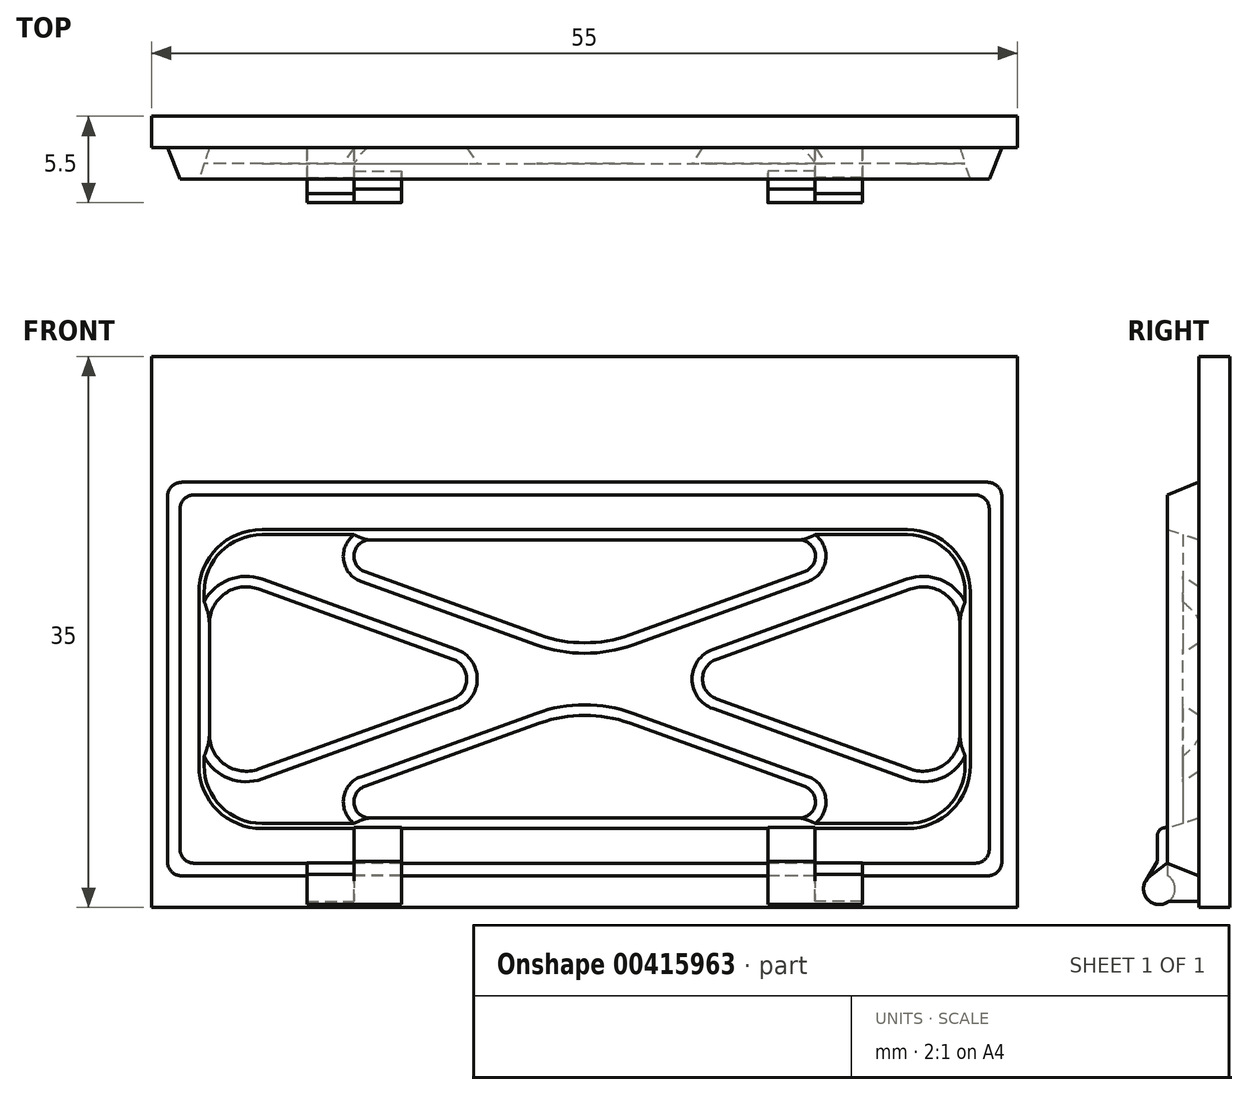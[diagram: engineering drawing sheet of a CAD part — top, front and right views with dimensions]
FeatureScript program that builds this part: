
annotation { "Feature Type Name" : "Feature", "Feature Type Description" : "" }
export const myFeature = defineFeature(function(context is Context, id is Id, definition is map)
    precondition{}
    {
        {
            var Q0;
            Q0=qCreatedBy(makeId("Front.planeOp"),FACE);
            var sketch = newSketch(context, id + "F0", { "sketchPlane" : qUnion([Q0])});
            skLineSegment(sketch, "E0.bottom", {"start": v(-23.45, 22) * mm, "end": v(31.55, 22) * mm});
            skLineSegment(sketch, "E0.top", {"start": v(-23.45, -13) * mm, "end": v(31.55, -13) * mm});
            skLineSegment(sketch, "E0.left", {"start": v(-23.45, 22) * mm, "end": v(-23.45, -13) * mm});
            skLineSegment(sketch, "E0.right", {"start": v(31.55, 22) * mm, "end": v(31.55, -13) * mm});
            skSolve(sketch);
        }
        {
            var Q0;
            Q0=makeQuery(id+"F0.imprint","IMPRINT",FACE,{"disambiguationData":[TD([[makeQuery(id+"F0.imprint","IMPRINT",EDGE,{"derivedFrom":sQuery(id+"F0.wireOp",EDGE,"E0.bottom")}),-1.0]])]});
            extrude(context, id + "F1", {"entities" : qUnion([Q0]), "depth" : 2 * mm, "offsetDistance" : 25 * mm});
        }
        {
            var Q0;
            Q0=makeQuery(id+"F1.opExtrude","CAP_FACE",FACE,{"disambiguationData":[OSD([sQuery(id+"F0.wireOp",EDGE,"E0.bottom"),sQuery(id+"F0.wireOp",EDGE,"E0.top"),sQuery(id+"F0.wireOp",EDGE,"E0.left"),sQuery(id+"F0.wireOp",EDGE,"E0.right")])],"isStart":false});
            var sketch = newSketch(context, id + "F2", { "sketchPlane" : qUnion([Q0])});
            skLineSegment(sketch, "E1", {"start": v(30.55, -11) * mm, "end": v(30.55, 14) * mm});
            skLineSegment(sketch, "E2", {"start": v(-22.45, -11) * mm, "end": v(-22.45, 14) * mm});
            skLineSegment(sketch, "E3", {"start": v(-22.45, 14) * mm, "end": v(30.55, 14) * mm});
            skLineSegment(sketch, "E4", {"start": v(30.55, -11) * mm, "end": v(-22.45, -11) * mm});
            skLineSegment(sketch, "E5.0", {"start": v(-19.45, 10) * mm, "end": v(27.55, 10) * mm});
            skLineSegment(sketch, "E6.0", {"start": v(-19.45, -7) * mm, "end": v(27.55, -7) * mm});
            skLineSegment(sketch, "E7.0", {"start": v(-19.45, 10) * mm, "end": v(-19.45, -7) * mm});
            skLineSegment(sketch, "E8.0", {"start": v(27.55, -7) * mm, "end": v(27.55, 10) * mm});
            skSolve(sketch);
        }
        {
            var Q0;
            Q0=makeQuery(id+"F2.imprint","IMPRINT",FACE,{"disambiguationData":[TD([[makeQuery(id+"F2.imprint","IMPRINT",EDGE,{"derivedFrom":sQuery(id+"F2.wireOp",EDGE,"E1")}),1.0]])]});
            extrude(context, id + "F3", {"entities" : qUnion([Q0]), "operationType" : NewBodyOperationType.ADD, "depth" : 2 * mm, "offsetDistance" : 25 * mm});
        }
        {
            var Q0;
            Q0=makeQuery(id+"F3.boolean.opBoolean","SPLIT",FACE,{"disambiguationData":[TD([makeQuery(id+"F3.opExtrude","SWEPT_FACE",FACE,{"disambiguationData":[OSD([sQuery(id+"F2.wireOp",EDGE,"E5.0")])]})])],"derivedFrom":makeQuery(id+"F1.opExtrude","CAP_FACE",FACE,{"disambiguationData":[OSD([sQuery(id+"F0.wireOp",EDGE,"E0.bottom"),sQuery(id+"F0.wireOp",EDGE,"E0.top"),sQuery(id+"F0.wireOp",EDGE,"E0.left"),sQuery(id+"F0.wireOp",EDGE,"E0.right")])],"isStart":false})});
            var sketch = newSketch(context, id + "F4", { "sketchPlane" : qUnion([Q0])});
            skLineSegment(sketch, "E9.bottom", {"start": v(-19.45, 10) * mm, "end": v(27.55, 10) * mm});
            skLineSegment(sketch, "E9.top", {"start": v(-19.45, -7) * mm, "end": v(27.55, -7) * mm});
            skLineSegment(sketch, "E9.left", {"start": v(-19.45, 10) * mm, "end": v(-19.45, -7) * mm});
            skLineSegment(sketch, "E9.right", {"start": v(27.55, 10) * mm, "end": v(27.55, -7) * mm});
            skLineSegment(sketch, "E10", {"start": v(-19.45, 10) * mm, "end": v(27.55, -7) * mm});
            skLineSegment(sketch, "E11", {"start": v(27.55, 10) * mm, "end": v(-19.45, -7) * mm});
            skLineSegment(sketch, "E12.0", {"start": v(-19.45, 7.87) * mm, "end": v(21.67, -7) * mm});
            skLineSegment(sketch, "E13.0", {"start": v(-13.57, 10) * mm, "end": v(27.55, -4.87) * mm});
            skLineSegment(sketch, "E14.0", {"start": v(21.67, 10) * mm, "end": v(-19.45, -4.87) * mm});
            skLineSegment(sketch, "E15.0", {"start": v(27.55, 7.87) * mm, "end": v(-13.57, -7) * mm});
            skLineSegment(sketch, "E16.0", {"start": v(-20.45, 11) * mm, "end": v(28.55, 11) * mm});
            skLineSegment(sketch, "E16.1", {"start": v(-20.45, 11) * mm, "end": v(-20.45, -8) * mm});
            skLineSegment(sketch, "E16.2", {"start": v(-20.45, -8) * mm, "end": v(28.55, -8) * mm});
            skLineSegment(sketch, "E16.3", {"start": v(28.55, 11) * mm, "end": v(28.55, -8) * mm});
            skSolve(sketch);
        }
        {
            var Q0;
            {var subQ1=sQuery(id+"F4.wireOp",EDGE,"E9.left");var subQ3=sQuery(id+"F4.wireOp",EDGE,"E12.0");var subQ4=makeQuery(id+"F4.imprint","INTERSECT",VERTEX,{"derivedFrom":[subQ1,subQ3]});Q0=makeQuery(id+"F4.imprint","IMPRINT",FACE,{"disambiguationData":[TD([[makeQuery(id+"F4.imprint","IMPRINT",EDGE,{"disambiguationData":[TD([[subQ4,-1.0]])],"derivedFrom":subQ3}),1.0]])]});}
            var Q1;
            {var subQ1=sQuery(id+"F4.wireOp",EDGE,"E9.bottom");var subQ3=sQuery(id+"F4.wireOp",EDGE,"E13.0");var subQ4=makeQuery(id+"F4.imprint","INTERSECT",VERTEX,{"derivedFrom":[subQ1,subQ3]});Q1=makeQuery(id+"F4.imprint","IMPRINT",FACE,{"disambiguationData":[TD([[makeQuery(id+"F4.imprint","IMPRINT",EDGE,{"disambiguationData":[TD([[subQ4,-1.0]])],"derivedFrom":subQ3}),-1.0]])]});}
            var Q2;
            {var subQ0=sQuery(id+"F4.wireOp",EDGE,"E14.0");var subQ1=sQuery(id+"F4.wireOp",EDGE,"E10");var subQ2=makeQuery(id+"F4.imprint","INTERSECT",VERTEX,{"derivedFrom":[subQ1,subQ0]});Q2=makeQuery(id+"F4.imprint","IMPRINT",FACE,{"disambiguationData":[TD([[makeQuery(id+"F4.imprint","IMPRINT",EDGE,{"disambiguationData":[TD([[subQ2,-1.0]])],"derivedFrom":subQ1}),1.0]])]});}
            var Q3;
            {var subQ0=sQuery(id+"F4.wireOp",EDGE,"E11");var subQ1=sQuery(id+"F4.wireOp",EDGE,"E10");var subQ2=makeQuery(id+"F4.imprint","INTERSECT",VERTEX,{"derivedFrom":[subQ1,subQ0]});Q3=makeQuery(id+"F4.imprint","IMPRINT",FACE,{"disambiguationData":[TD([[makeQuery(id+"F4.imprint","IMPRINT",EDGE,{"disambiguationData":[TD([[subQ2,-1.0]])],"derivedFrom":subQ1}),-1.0]])]});}
            var Q4;
            {var subQ0=sQuery(id+"F4.wireOp",EDGE,"E11");var subQ1=sQuery(id+"F4.wireOp",EDGE,"E10");var subQ2=makeQuery(id+"F4.imprint","INTERSECT",VERTEX,{"derivedFrom":[subQ1,subQ0]});Q4=makeQuery(id+"F4.imprint","IMPRINT",FACE,{"disambiguationData":[TD([[makeQuery(id+"F4.imprint","IMPRINT",EDGE,{"disambiguationData":[TD([[subQ2,-1.0]])],"derivedFrom":subQ1}),1.0]])]});}
            var Q5;
            {var subQ0=sQuery(id+"F4.wireOp",EDGE,"E14.0");var subQ1=sQuery(id+"F4.wireOp",EDGE,"E10");var subQ2=makeQuery(id+"F4.imprint","INTERSECT",VERTEX,{"derivedFrom":[subQ1,subQ0]});Q5=makeQuery(id+"F4.imprint","IMPRINT",FACE,{"disambiguationData":[TD([[makeQuery(id+"F4.imprint","IMPRINT",EDGE,{"disambiguationData":[TD([[subQ2,-1.0]])],"derivedFrom":subQ1}),-1.0]])]});}
            var Q6;
            {var subQ0=sQuery(id+"F4.wireOp",EDGE,"E11");var subQ5=sQuery(id+"F4.wireOp",EDGE,"E12.0");var subQ6=makeQuery(id+"F4.imprint","INTERSECT",VERTEX,{"derivedFrom":[subQ0,subQ5]});Q6=makeQuery(id+"F4.imprint","IMPRINT",FACE,{"disambiguationData":[TD([[makeQuery(id+"F4.imprint","IMPRINT",EDGE,{"disambiguationData":[TD([[subQ6,-1.0]])],"derivedFrom":subQ5}),-1.0]])]});}
            var Q7;
            {var subQ0=sQuery(id+"F4.wireOp",EDGE,"E11");var subQ5=sQuery(id+"F4.wireOp",EDGE,"E13.0");var subQ6=makeQuery(id+"F4.imprint","INTERSECT",VERTEX,{"derivedFrom":[subQ0,subQ5]});Q7=makeQuery(id+"F4.imprint","IMPRINT",FACE,{"disambiguationData":[TD([[makeQuery(id+"F4.imprint","IMPRINT",EDGE,{"disambiguationData":[TD([[subQ6,1.0]])],"derivedFrom":subQ5}),1.0]])]});}
            var Q8;
            {var subQ0=sQuery(id+"F4.wireOp",EDGE,"E11");var subQ5=sQuery(id+"F4.wireOp",EDGE,"E13.0");var subQ6=makeQuery(id+"F4.imprint","INTERSECT",VERTEX,{"derivedFrom":[subQ0,subQ5]});Q8=makeQuery(id+"F4.imprint","IMPRINT",FACE,{"disambiguationData":[TD([[makeQuery(id+"F4.imprint","IMPRINT",EDGE,{"disambiguationData":[TD([[subQ6,-1.0]])],"derivedFrom":subQ5}),1.0]])]});}
            var Q9;
            {var subQ1=sQuery(id+"F4.wireOp",EDGE,"E9.right");var subQ3=sQuery(id+"F4.wireOp",EDGE,"E13.0");var subQ4=makeQuery(id+"F4.imprint","INTERSECT",VERTEX,{"derivedFrom":[subQ1,subQ3]});Q9=makeQuery(id+"F4.imprint","IMPRINT",FACE,{"disambiguationData":[TD([[makeQuery(id+"F4.imprint","IMPRINT",EDGE,{"disambiguationData":[TD([[subQ4,1.0]])],"derivedFrom":subQ3}),-1.0]])]});}
            var Q10;
            {var subQ1=sQuery(id+"F4.wireOp",EDGE,"E9.top");var subQ3=sQuery(id+"F4.wireOp",EDGE,"E12.0");var subQ4=makeQuery(id+"F4.imprint","INTERSECT",VERTEX,{"derivedFrom":[subQ1,subQ3]});Q10=makeQuery(id+"F4.imprint","IMPRINT",FACE,{"disambiguationData":[TD([[makeQuery(id+"F4.imprint","IMPRINT",EDGE,{"disambiguationData":[TD([[subQ4,1.0]])],"derivedFrom":subQ3}),1.0]])]});}
            var Q11;
            {var subQ0=sQuery(id+"F4.wireOp",EDGE,"E11");var subQ5=sQuery(id+"F4.wireOp",EDGE,"E12.0");var subQ6=makeQuery(id+"F4.imprint","INTERSECT",VERTEX,{"derivedFrom":[subQ0,subQ5]});Q11=makeQuery(id+"F4.imprint","IMPRINT",FACE,{"disambiguationData":[TD([[makeQuery(id+"F4.imprint","IMPRINT",EDGE,{"disambiguationData":[TD([[subQ6,1.0]])],"derivedFrom":subQ5}),-1.0]])]});}
            var Q12;
            Q12=makeQuery(id+"F4.imprint","IMPRINT",FACE,{"disambiguationData":[TD([[makeQuery(id+"F4.imprint","IMPRINT",EDGE,{"derivedFrom":sQuery(id+"F4.wireOp",EDGE,"E16.0")}),-1.0]])]});
            extrude(context, id + "F5", {"entities" : qUnion([Q0, Q1, Q2, Q3, Q4, Q5, Q6, Q7, Q8, Q9, Q10, Q11, Q12]), "depth" : 1 * mm, "offsetDistance" : 25 * mm});
        }
        {
            var Q0;
            Q0=makeQuery(id+"F5.opExtrude","SWEPT_EDGE",EDGE,{"disambiguationData":[OSD([sQuery(id+"F4.wireOp",EDGE,"E9.left"),sQuery(id+"F4.wireOp",EDGE,"E12.0")])]});
            var Q1;
            Q1=makeQuery(id+"F5.opExtrude","SWEPT_EDGE",EDGE,{"disambiguationData":[OSD([sQuery(id+"F4.wireOp",EDGE,"E9.left"),sQuery(id+"F4.wireOp",EDGE,"E14.0")])]});
            var Q2;
            Q2=makeQuery(id+"F5.opExtrude","SWEPT_EDGE",EDGE,{"disambiguationData":[OSD([sQuery(id+"F4.wireOp",EDGE,"E9.right"),sQuery(id+"F4.wireOp",EDGE,"E13.0")])]});
            var Q3;
            Q3=makeQuery(id+"F5.opExtrude","SWEPT_EDGE",EDGE,{"disambiguationData":[OSD([sQuery(id+"F4.wireOp",EDGE,"E9.right"),sQuery(id+"F4.wireOp",EDGE,"E15.0")])]});
            fillet(context, id + "F6", {"entities" : qUnion([Q0, Q1, Q2, Q3]), "radius" : 2 * mm, "tangentPropagation" : true, "allowEdgeOverflow" : false});
        }
        {
            var Q0;
            Q0=makeQuery(id+"F5.opExtrude","SWEPT_EDGE",EDGE,{"disambiguationData":[OSD([sQuery(id+"F4.wireOp",EDGE,"E9.bottom"),sQuery(id+"F4.wireOp",EDGE,"E13.0")])]});
            var Q1;
            Q1=makeQuery(id+"F5.opExtrude","SWEPT_EDGE",EDGE,{"disambiguationData":[OSD([sQuery(id+"F4.wireOp",EDGE,"E9.top"),sQuery(id+"F4.wireOp",EDGE,"E15.0")])]});
            var Q2;
            Q2=makeQuery(id+"F5.opExtrude","SWEPT_EDGE",EDGE,{"disambiguationData":[OSD([sQuery(id+"F4.wireOp",EDGE,"E9.top"),sQuery(id+"F4.wireOp",EDGE,"E12.0")])]});
            var Q3;
            Q3=makeQuery(id+"F5.opExtrude","SWEPT_EDGE",EDGE,{"disambiguationData":[OSD([sQuery(id+"F4.wireOp",EDGE,"E9.bottom"),sQuery(id+"F4.wireOp",EDGE,"E14.0")])]});
            fillet(context, id + "F7", {"entities" : qUnion([Q0, Q1, Q2, Q3]), "radius" : 0.7 * mm, "tangentPropagation" : true, "allowEdgeOverflow" : false});
        }
        {
            var Q0;
            Q0=makeQuery(id+"F5.opExtrude","SWEPT_EDGE",EDGE,{"disambiguationData":[OSD([sQuery(id+"F4.wireOp",EDGE,"E13.0"),sQuery(id+"F4.wireOp",EDGE,"E14.0")])]});
            var Q1;
            Q1=makeQuery(id+"F5.opExtrude","SWEPT_EDGE",EDGE,{"disambiguationData":[OSD([sQuery(id+"F4.wireOp",EDGE,"E12.0"),sQuery(id+"F4.wireOp",EDGE,"E15.0")])]});
            fillet(context, id + "F8", {"entities" : qUnion([Q0, Q1]), "radius" : 8 * mm, "tangentPropagation" : true, "allowEdgeOverflow" : false});
        }
        {
            var Q0;
            Q0=makeQuery(id+"F5.opExtrude","SWEPT_EDGE",EDGE,{"disambiguationData":[OSD([sQuery(id+"F4.wireOp",EDGE,"E12.0"),sQuery(id+"F4.wireOp",EDGE,"E14.0")])]});
            var Q1;
            Q1=makeQuery(id+"F5.opExtrude","SWEPT_EDGE",EDGE,{"disambiguationData":[OSD([sQuery(id+"F4.wireOp",EDGE,"E13.0"),sQuery(id+"F4.wireOp",EDGE,"E15.0")])]});
            fillet(context, id + "F9", {"entities" : qUnion([Q0, Q1]), "radius" : 1 * mm, "tangentPropagation" : true, "allowEdgeOverflow" : false});
        }
        {
            var Q0;
            {var subQ0=sQuery(id+"F4.wireOp",EDGE,"E13.0");Q0=makeQuery(id+"F5.opExtrude","CAP_EDGE",EDGE,{"disambiguationData":[OSD([subQ0]),TDD([makeQuery(id+"F4.imprint","IMPRINT",EDGE,{"disambiguationData":[TD([[makeQuery(id+"F4.imprint","INTERSECT",VERTEX,{"derivedFrom":[sQuery(id+"F4.wireOp",EDGE,"E9.bottom"),subQ0]}),-1.0]])],"derivedFrom":subQ0})])],"isStart":false});}
            var Q1;
            {var subQ0=sQuery(id+"F4.wireOp",EDGE,"E12.0");Q1=makeQuery(id+"F5.opExtrude","CAP_EDGE",EDGE,{"disambiguationData":[OSD([subQ0]),TDD([makeQuery(id+"F4.imprint","IMPRINT",EDGE,{"disambiguationData":[TD([[makeQuery(id+"F4.imprint","INTERSECT",VERTEX,{"derivedFrom":[sQuery(id+"F4.wireOp",EDGE,"E9.left"),subQ0]}),-1.0]])],"derivedFrom":subQ0})])],"isStart":false});}
            var Q2;
            {var subQ0=sQuery(id+"F4.wireOp",EDGE,"E15.0");Q2=makeQuery(id+"F5.opExtrude","CAP_EDGE",EDGE,{"disambiguationData":[OSD([subQ0]),TDD([makeQuery(id+"F4.imprint","IMPRINT",EDGE,{"disambiguationData":[TD([[makeQuery(id+"F4.imprint","INTERSECT",VERTEX,{"derivedFrom":[sQuery(id+"F4.wireOp",EDGE,"E9.top"),subQ0]}),1.0]])],"derivedFrom":subQ0})])],"isStart":false});}
            var Q3;
            {var subQ0=sQuery(id+"F4.wireOp",EDGE,"E13.0");Q3=makeQuery(id+"F5.opExtrude","CAP_EDGE",EDGE,{"disambiguationData":[OSD([subQ0]),TDD([makeQuery(id+"F4.imprint","IMPRINT",EDGE,{"disambiguationData":[TD([[makeQuery(id+"F4.imprint","INTERSECT",VERTEX,{"derivedFrom":[sQuery(id+"F4.wireOp",EDGE,"E9.right"),subQ0]}),1.0]])],"derivedFrom":subQ0})])],"isStart":false});}
            chamfer(context, id + "F10", {"entities" : qUnion([Q0, Q1, Q2, Q3]), "chamferType" : ChamferType.TWO_OFFSETS, "width1" : 1 * mm, "oppositeDirection" : true, "width2" : 1.5 * mm, "tangentPropagation" : true});
        }
        {
            var Q0;
            Q0=makeQuery(id+"F3.opExtrude","SWEPT_EDGE",EDGE,{"disambiguationData":[OSD([sQuery(id+"F2.wireOp",EDGE,"E5.0"),sQuery(id+"F2.wireOp",EDGE,"E7.0")])]});
            var Q1;
            Q1=makeQuery(id+"F3.opExtrude","SWEPT_EDGE",EDGE,{"disambiguationData":[OSD([sQuery(id+"F2.wireOp",EDGE,"E5.0"),sQuery(id+"F2.wireOp",EDGE,"E8.0")])]});
            var Q2;
            Q2=makeQuery(id+"F3.opExtrude","SWEPT_EDGE",EDGE,{"disambiguationData":[OSD([sQuery(id+"F2.wireOp",EDGE,"E6.0"),sQuery(id+"F2.wireOp",EDGE,"E8.0")])]});
            var Q3;
            Q3=makeQuery(id+"F3.opExtrude","SWEPT_EDGE",EDGE,{"disambiguationData":[OSD([sQuery(id+"F2.wireOp",EDGE,"E6.0"),sQuery(id+"F2.wireOp",EDGE,"E7.0")])]});
            fillet(context, id + "F11", {"entities" : qUnion([Q0, Q1, Q2, Q3]), "radius" : 3 * mm, "tangentPropagation" : true, "allowEdgeOverflow" : false});
        }
        {
            var Q0;
            Q0=makeQuery(id+"F3.opExtrude","CAP_EDGE",EDGE,{"disambiguationData":[OSD([sQuery(id+"F2.wireOp",EDGE,"E5.0")])],"isStart":false});
            chamfer(context, id + "F12", {"entities" : qUnion([Q0]), "chamferType" : ChamferType.TWO_OFFSETS, "width1" : 1 * mm, "oppositeDirection" : false, "width2" : 3 * mm, "tangentPropagation" : true});
        }
        {
            var Q0;
            Q0=makeQuery(id+"F3.opExtrude","CAP_EDGE",EDGE,{"disambiguationData":[OSD([sQuery(id+"F2.wireOp",EDGE,"E2")])],"isStart":false});
            var Q1;
            Q1=makeQuery(id+"F3.opExtrude","CAP_EDGE",EDGE,{"disambiguationData":[OSD([sQuery(id+"F2.wireOp",EDGE,"E3")])],"isStart":false});
            var Q2;
            Q2=makeQuery(id+"F3.opExtrude","CAP_EDGE",EDGE,{"disambiguationData":[OSD([sQuery(id+"F2.wireOp",EDGE,"E1")])],"isStart":false});
            var Q3;
            Q3=makeQuery(id+"F3.opExtrude","CAP_EDGE",EDGE,{"disambiguationData":[OSD([sQuery(id+"F2.wireOp",EDGE,"E4")])],"isStart":false});
            chamfer(context, id + "F13", {"entities" : qUnion([Q0, Q1, Q2, Q3]), "chamferType" : ChamferType.TWO_OFFSETS, "width1" : 2 * mm, "oppositeDirection" : false, "width2" : 0.8 * mm, "tangentPropagation" : true});
        }
        {
            var Q0;
            Q0=makeQuery(id+"F13.opChamfer","BLEND_EDGE",EDGE,{"blendedFrom":[makeQuery(id+"F3.opExtrude","CAP_EDGE",EDGE,{"disambiguationData":[OSD([sQuery(id+"F2.wireOp",EDGE,"E2")])],"isStart":false}),makeQuery(id+"F3.opExtrude","CAP_EDGE",EDGE,{"disambiguationData":[OSD([sQuery(id+"F2.wireOp",EDGE,"E3")])],"isStart":false})],"blendedInto":[]});
            var Q1;
            Q1=makeQuery(id+"F13.opChamfer","BLEND_EDGE",EDGE,{"blendedFrom":[makeQuery(id+"F3.opExtrude","CAP_EDGE",EDGE,{"disambiguationData":[OSD([sQuery(id+"F2.wireOp",EDGE,"E1")])],"isStart":false}),makeQuery(id+"F3.opExtrude","CAP_EDGE",EDGE,{"disambiguationData":[OSD([sQuery(id+"F2.wireOp",EDGE,"E3")])],"isStart":false})],"blendedInto":[]});
            var Q2;
            Q2=makeQuery(id+"F13.opChamfer","BLEND_EDGE",EDGE,{"blendedFrom":[makeQuery(id+"F3.opExtrude","CAP_EDGE",EDGE,{"disambiguationData":[OSD([sQuery(id+"F2.wireOp",EDGE,"E1")])],"isStart":false}),makeQuery(id+"F3.opExtrude","CAP_EDGE",EDGE,{"disambiguationData":[OSD([sQuery(id+"F2.wireOp",EDGE,"E4")])],"isStart":false})],"blendedInto":[]});
            var Q3;
            Q3=makeQuery(id+"F13.opChamfer","BLEND_EDGE",EDGE,{"blendedFrom":[makeQuery(id+"F3.opExtrude","CAP_EDGE",EDGE,{"disambiguationData":[OSD([sQuery(id+"F2.wireOp",EDGE,"E2")])],"isStart":false}),makeQuery(id+"F3.opExtrude","CAP_EDGE",EDGE,{"disambiguationData":[OSD([sQuery(id+"F2.wireOp",EDGE,"E4")])],"isStart":false})],"blendedInto":[]});
            fillet(context, id + "F14", {"entities" : qUnion([Q0, Q1, Q2, Q3]), "radius" : 1 * mm, "tangentPropagation" : true, "allowEdgeOverflow" : false});
        }
        {
            var Q0;
            Q0=makeQuery(id+"F1.opExtrude","SWEPT_BODY",BODY,{"disambiguationData":[OSD([sQuery(id+"F0.wireOp",EDGE,"E0.bottom"),sQuery(id+"F0.wireOp",EDGE,"E0.top"),sQuery(id+"F0.wireOp",EDGE,"E0.left"),sQuery(id+"F0.wireOp",EDGE,"E0.right")])]});
            var Q1;
            Q1=makeQuery(id+"F5.opExtrude","SWEPT_BODY",BODY,{"disambiguationData":[OSD([sQuery(id+"F4.wireOp",EDGE,"E9.bottom"),sQuery(id+"F4.wireOp",EDGE,"E9.top"),sQuery(id+"F4.wireOp",EDGE,"E9.left"),sQuery(id+"F4.wireOp",EDGE,"E9.right"),sQuery(id+"F4.wireOp",EDGE,"E12.0"),sQuery(id+"F4.wireOp",EDGE,"E13.0"),sQuery(id+"F4.wireOp",EDGE,"E14.0"),sQuery(id+"F4.wireOp",EDGE,"E15.0"),sQuery(id+"F4.wireOp",EDGE,"E16.0"),sQuery(id+"F4.wireOp",EDGE,"E16.1"),sQuery(id+"F4.wireOp",EDGE,"E16.2"),sQuery(id+"F4.wireOp",EDGE,"E16.3")])]});
            booleanBodies(context, id + "F15", {"operationType" : BooleanOperationType.UNION, "tools" : qUnion([Q0, Q1])});
        }
        {
            var Q0;
            Q0=qCreatedBy(makeId("Right.planeOp"),FACE);
            var Q1;
            {var subQ0=sQuery(id+"F4.wireOp",EDGE,"E16.3");var subQ1=sQuery(id+"F4.wireOp",EDGE,"E16.2");var subQ2=sQuery(id+"F4.wireOp",EDGE,"E16.1");var subQ3=sQuery(id+"F4.wireOp",EDGE,"E16.0");var subQ4=sQuery(id+"F4.wireOp",EDGE,"E15.0");var subQ5=sQuery(id+"F4.wireOp",EDGE,"E14.0");var subQ6=sQuery(id+"F4.wireOp",EDGE,"E13.0");var subQ7=sQuery(id+"F4.wireOp",EDGE,"E12.0");var subQ8=sQuery(id+"F4.wireOp",EDGE,"E9.right");var subQ9=sQuery(id+"F4.wireOp",EDGE,"E9.left");var subQ10=sQuery(id+"F4.wireOp",EDGE,"E9.top");var subQ11=sQuery(id+"F4.wireOp",EDGE,"E9.bottom");var subQ12=makeQuery(id+"F5.opExtrude","CAP_FACE",FACE,{"disambiguationData":[OSD([subQ11,subQ10,subQ9,subQ8,subQ7,subQ6,subQ5,subQ4,subQ3,subQ2,subQ1,subQ0])],"isStart":false});Q1=makeQuery(id+"F15.opBoolean","INTERSECT",VERTEX,{"derivedFrom":[makeQuery(id+"F10.opChamfer","BLEND_FACE",FACE,{"disambiguationData":[OSD([subQ11,subQ10,subQ9,subQ8,subQ7,subQ6,subQ5,subQ4,subQ3,subQ2,subQ1,subQ0]),TDD([makeQuery(id+"F7.opFillet","BLEND_EDGE",EDGE,{"blendedFrom":[makeQuery(id+"F5.opExtrude","SWEPT_EDGE",EDGE,{"disambiguationData":[OSD([subQ10,subQ4])]}),subQ12],"blendedInto":[subQ12]})])]}),subQ12,makeQuery(id+"F12.opChamfer","BLEND_FACE",FACE,{"disambiguationData":[OSD([sQuery(id+"F2.wireOp",EDGE,"E6.0")])]})]});}
            cPlane(context, id + "F16", {"entities" : qUnion([Q0, Q1]), "cplaneType" : CPlaneType.PLANE_POINT, "offset" : 25 * mm, "width" : 150 * mm, "height" : 150 * mm});
        }
        {
            var Q0;
            Q0=qCreatedBy(id+"F16.planeOp",FACE);
            var sketch = newSketch(context, id + "F17", { "sketchPlane" : qUnion([Q0])});
            skCircle(sketch, "E17", {"center": v(-4.5, -11.83) * mm, "radius": 1 * mm});
            skLineSegment(sketch, "E18", {"start": v(-3.94, -11) * mm, "end": v(-2, -11) * mm});
            skLineSegment(sketch, "E19", {"start": v(-2, -12.63) * mm, "end": v(-3.9, -12.63) * mm});
            skLineSegment(sketch, "E20", {"start": v(-4, -10.96) * mm, "end": v(-4, -10.18) * mm});
            skLineSegment(sketch, "E21", {"start": v(-4, -10.18) * mm, "end": v(-4, -7.94) * mm});
            skLineSegment(sketch, "E22", {"start": v(-4, -7.94) * mm, "end": v(-4.62, -7.94) * mm});
            skLineSegment(sketch, "E23", {"start": v(-4.62, -7.94) * mm, "end": v(-4.62, -10.07) * mm});
            skLineSegment(sketch, "E24", {"start": v(-4.62, -10.07) * mm, "end": v(-5.36, -11.32) * mm});
            skLineSegment(sketch, "E25", {"start": v(-2, -11) * mm, "end": v(-2, -12.63) * mm});
            skLineSegment(sketch, "E26", {"start": v(-2, -11) * mm, "end": v(-4, -10.18) * mm});
            skLineSegment(sketch, "E27", {"start": v(-4, -10.18) * mm, "end": v(-4.93, -10.92) * mm});
            skSolve(sketch);
        }
        {
            var Q0;
            {var subQ0=sQuery(id+"F17.wireOp",EDGE,"E17");var subQ1=makeQuery(id+"F17.imprint","INTERSECT",VERTEX,{"derivedFrom":[subQ0,sQuery(id+"F17.wireOp",EDGE,"E18")]});Q0=makeQuery(id+"F17.imprint","IMPRINT",FACE,{"disambiguationData":[TD([[makeQuery(id+"F17.imprint","IMPRINT",EDGE,{"disambiguationData":[TD([[subQ1,-1.0]])],"derivedFrom":subQ0}),1.0]])]});}
            var Q1;
            {var subQ0=sQuery(id+"F17.wireOp",EDGE,"E18");Q1=makeQuery(id+"F17.imprint","IMPRINT",FACE,{"disambiguationData":[TD([[makeQuery(id+"F17.imprint","IMPRINT",EDGE,{"derivedFrom":subQ0}),-1.0]])]});}
            var Q2;
            {var subQ0=sQuery(id+"F17.wireOp",EDGE,"E18");Q2=makeQuery(id+"F17.imprint","IMPRINT",FACE,{"disambiguationData":[TD([[makeQuery(id+"F17.imprint","IMPRINT",EDGE,{"derivedFrom":subQ0}),1.0]])]});}
            var Q3;
            {var subQ0=sQuery(id+"F17.wireOp",EDGE,"E20");Q3=makeQuery(id+"F17.imprint","IMPRINT",FACE,{"disambiguationData":[TD([[makeQuery(id+"F17.imprint","IMPRINT",EDGE,{"derivedFrom":subQ0}),1.0]])]});}
            extrude(context, id + "F18", {"entities" : qUnion([Q0, Q1, Q2, Q3]), "operationType" : NewBodyOperationType.ADD, "oppositeDirection" : true, "depth" : 3 * mm, "offsetDistance" : 25 * mm});
        }
        {
            var Q0;
            {var subQ0=sQuery(id+"F17.wireOp",EDGE,"E20");Q0=makeQuery(id+"F17.imprint","IMPRINT",FACE,{"disambiguationData":[TD([[makeQuery(id+"F17.imprint","IMPRINT",EDGE,{"derivedFrom":subQ0}),1.0]])]});}
            var Q1;
            {var subQ0=sQuery(id+"F17.wireOp",EDGE,"E17");var subQ1=makeQuery(id+"F17.imprint","INTERSECT",VERTEX,{"derivedFrom":[subQ0,sQuery(id+"F17.wireOp",EDGE,"E18")]});Q1=makeQuery(id+"F17.imprint","IMPRINT",FACE,{"disambiguationData":[TD([[makeQuery(id+"F17.imprint","IMPRINT",EDGE,{"disambiguationData":[TD([[subQ1,-1.0]])],"derivedFrom":subQ0}),1.0]])]});}
            var Q2;
            Q2=makeQuery(id+"F17.imprint","IMPRINT",FACE,{"disambiguationData":[TD([[makeQuery(id+"F17.imprint","IMPRINT",EDGE,{"derivedFrom":sQuery(id+"F17.wireOp",EDGE,"E21")}),1.0]])]});
            extrude(context, id + "F19", {"entities" : qUnion([Q0, Q1, Q2]), "operationType" : NewBodyOperationType.ADD, "depth" : 3 * mm, "offsetDistance" : 25 * mm});
        }
        {
            var Q0;
            Q0=qCreatedBy(makeId("Right.planeOp"),FACE);
            var Q1;
            {var subQ0=sQuery(id+"F4.wireOp",EDGE,"E16.3");var subQ1=sQuery(id+"F4.wireOp",EDGE,"E16.2");var subQ2=sQuery(id+"F4.wireOp",EDGE,"E16.1");var subQ3=sQuery(id+"F4.wireOp",EDGE,"E16.0");var subQ4=sQuery(id+"F4.wireOp",EDGE,"E15.0");var subQ5=sQuery(id+"F4.wireOp",EDGE,"E14.0");var subQ6=sQuery(id+"F4.wireOp",EDGE,"E13.0");var subQ7=sQuery(id+"F4.wireOp",EDGE,"E12.0");var subQ8=sQuery(id+"F4.wireOp",EDGE,"E9.right");var subQ9=sQuery(id+"F4.wireOp",EDGE,"E9.left");var subQ10=sQuery(id+"F4.wireOp",EDGE,"E9.top");var subQ11=sQuery(id+"F4.wireOp",EDGE,"E9.bottom");var subQ12=makeQuery(id+"F5.opExtrude","CAP_FACE",FACE,{"disambiguationData":[OSD([subQ11,subQ10,subQ9,subQ8,subQ7,subQ6,subQ5,subQ4,subQ3,subQ2,subQ1,subQ0])],"isStart":false});Q1=makeQuery(id+"F15.opBoolean","INTERSECT",VERTEX,{"derivedFrom":[makeQuery(id+"F10.opChamfer","BLEND_FACE",FACE,{"disambiguationData":[OSD([subQ11,subQ10,subQ9,subQ8,subQ7,subQ6,subQ5,subQ4,subQ3,subQ2,subQ1,subQ0]),TDD([makeQuery(id+"F7.opFillet","BLEND_EDGE",EDGE,{"blendedFrom":[makeQuery(id+"F5.opExtrude","SWEPT_EDGE",EDGE,{"disambiguationData":[OSD([subQ10,subQ7])]}),subQ12],"blendedInto":[subQ12]})])]}),subQ12,makeQuery(id+"F12.opChamfer","BLEND_FACE",FACE,{"disambiguationData":[OSD([sQuery(id+"F2.wireOp",EDGE,"E6.0")])]})]});}
            cPlane(context, id + "F20", {"entities" : qUnion([Q0, Q1]), "cplaneType" : CPlaneType.PLANE_POINT, "offset" : 25 * mm, "width" : 150 * mm, "height" : 150 * mm});
        }
        {
            var Q0;
            Q0=qCreatedBy(id+"F20.planeOp",FACE);
            var sketch = newSketch(context, id + "F21", { "sketchPlane" : qUnion([Q0])});
            skCircle(sketch, "E28", {"center": v(-4.5, -11.83) * mm, "radius": 1 * mm});
            skLineSegment(sketch, "E29", {"start": v(-3.94, -11) * mm, "end": v(-2, -11) * mm});
            skLineSegment(sketch, "E30", {"start": v(-2, -12.63) * mm, "end": v(-3.9, -12.63) * mm});
            skLineSegment(sketch, "E31", {"start": v(-4, -10.96) * mm, "end": v(-4, -10.18) * mm});
            skLineSegment(sketch, "E32", {"start": v(-4, -10.18) * mm, "end": v(-4, -7.94) * mm});
            skLineSegment(sketch, "E33", {"start": v(-4, -7.94) * mm, "end": v(-4.62, -7.94) * mm});
            skLineSegment(sketch, "E34", {"start": v(-4.62, -7.94) * mm, "end": v(-4.62, -10.07) * mm});
            skLineSegment(sketch, "E35", {"start": v(-4.62, -10.07) * mm, "end": v(-5.36, -11.32) * mm});
            skLineSegment(sketch, "E36", {"start": v(-2, -11) * mm, "end": v(-2, -12.63) * mm});
            skLineSegment(sketch, "E37", {"start": v(-2, -11) * mm, "end": v(-4, -10.18) * mm});
            skLineSegment(sketch, "E38", {"start": v(-4, -10.18) * mm, "end": v(-4.93, -10.92) * mm});
            skSolve(sketch);
        }
        {
            var Q0;
            {var subQ0=sQuery(id+"F21.wireOp",EDGE,"E29");Q0=makeQuery(id+"F21.imprint","IMPRINT",FACE,{"disambiguationData":[TD([[makeQuery(id+"F21.imprint","IMPRINT",EDGE,{"derivedFrom":subQ0}),-1.0]])]});}
            var Q1;
            {var subQ0=sQuery(id+"F21.wireOp",EDGE,"E28");var subQ5=makeQuery(id+"F21.imprint","INTERSECT",VERTEX,{"derivedFrom":[subQ0,sQuery(id+"F21.wireOp",EDGE,"E29")]});Q1=makeQuery(id+"F21.imprint","IMPRINT",FACE,{"disambiguationData":[TD([[makeQuery(id+"F21.imprint","IMPRINT",EDGE,{"disambiguationData":[TD([[subQ5,-1.0]])],"derivedFrom":subQ0}),1.0]])]});}
            var Q2;
            {var subQ0=sQuery(id+"F21.wireOp",EDGE,"E29");Q2=makeQuery(id+"F21.imprint","IMPRINT",FACE,{"disambiguationData":[TD([[makeQuery(id+"F21.imprint","IMPRINT",EDGE,{"derivedFrom":subQ0}),1.0]])]});}
            var Q3;
            {var subQ0=sQuery(id+"F21.wireOp",EDGE,"E31");Q3=makeQuery(id+"F21.imprint","IMPRINT",FACE,{"disambiguationData":[TD([[makeQuery(id+"F21.imprint","IMPRINT",EDGE,{"derivedFrom":subQ0}),1.0]])]});}
            extrude(context, id + "F22", {"entities" : qUnion([Q0, Q1, Q2, Q3]), "operationType" : NewBodyOperationType.ADD, "depth" : 3 * mm, "offsetDistance" : 25 * mm});
        }
        {
            var Q0;
            {var subQ0=sQuery(id+"F21.wireOp",EDGE,"E28");var subQ5=makeQuery(id+"F21.imprint","INTERSECT",VERTEX,{"derivedFrom":[subQ0,sQuery(id+"F21.wireOp",EDGE,"E29")]});Q0=makeQuery(id+"F21.imprint","IMPRINT",FACE,{"disambiguationData":[TD([[makeQuery(id+"F21.imprint","IMPRINT",EDGE,{"disambiguationData":[TD([[subQ5,-1.0]])],"derivedFrom":subQ0}),1.0]])]});}
            var Q1;
            {var subQ0=sQuery(id+"F21.wireOp",EDGE,"E31");Q1=makeQuery(id+"F21.imprint","IMPRINT",FACE,{"disambiguationData":[TD([[makeQuery(id+"F21.imprint","IMPRINT",EDGE,{"derivedFrom":subQ0}),1.0]])]});}
            var Q2;
            Q2=makeQuery(id+"F21.imprint","IMPRINT",FACE,{"disambiguationData":[TD([[makeQuery(id+"F21.imprint","IMPRINT",EDGE,{"derivedFrom":sQuery(id+"F21.wireOp",EDGE,"E32")}),1.0]])]});
            extrude(context, id + "F23", {"entities" : qUnion([Q0, Q1, Q2]), "operationType" : NewBodyOperationType.ADD, "oppositeDirection" : true, "depth" : 3 * mm, "offsetDistance" : 25 * mm});
        }
        {
            var Q0;
            Q0=makeQuery(id+"F19.opExtrude","SWEPT_EDGE",EDGE,{"disambiguationData":[OSD([sQuery(id+"F17.wireOp",EDGE,"E22"),sQuery(id+"F17.wireOp",EDGE,"E23")])]});
            var Q1;
            Q1=makeQuery(id+"F23.opExtrude","SWEPT_EDGE",EDGE,{"disambiguationData":[OSD([sQuery(id+"F21.wireOp",EDGE,"E33"),sQuery(id+"F21.wireOp",EDGE,"E34")])]});
            fillet(context, id + "F24", {"entities" : qUnion([Q0, Q1]), "radius" : 0.5 * mm, "tangentPropagation" : true, "allowEdgeOverflow" : false});
        }
    });
